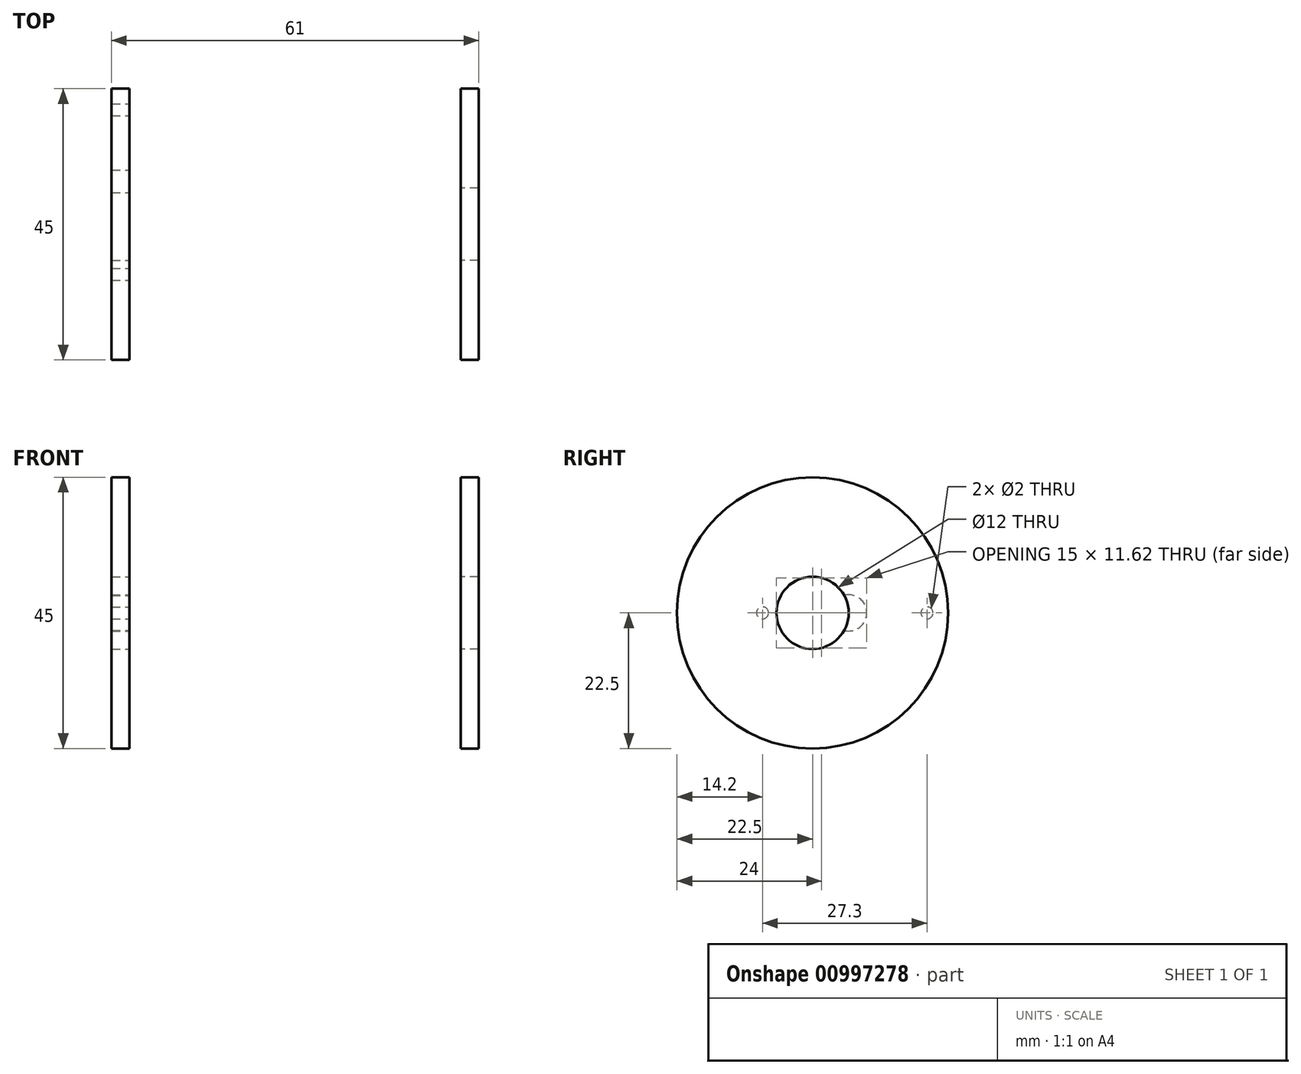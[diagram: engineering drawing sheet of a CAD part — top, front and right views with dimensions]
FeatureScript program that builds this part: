
annotation { "Feature Type Name" : "Feature", "Feature Type Description" : "" }
export const myFeature = defineFeature(function(context is Context, id is Id, definition is map)
    precondition{}
    {
        {
            var Q0;
            Q0=qCreatedBy(makeId("Front.planeOp"),FACE);
            var sketch = newSketch(context, id + "F0", { "sketchPlane" : qUnion([Q0])});
            skLineSegment(sketch, "E0.bottom", {"start": v(-27.5, 22.5) * mm, "end": v(27.5, 22.5) * mm});
            skLineSegment(sketch, "E0.top", {"start": v(-27.5, -22.5) * mm, "end": v(27.5, -22.5) * mm});
            skLineSegment(sketch, "E0.left", {"start": v(-27.5, 22.5) * mm, "end": v(-27.5, -22.5) * mm});
            skLineSegment(sketch, "E0.right", {"start": v(27.5, 22.5) * mm, "end": v(27.5, -22.5) * mm});
            skSolve(sketch);
        }
        {
            var Q0;
            Q0=qCreatedBy(makeId("Front.planeOp"),FACE);
            var sketch = newSketch(context, id + "F1", { "sketchPlane" : qUnion([Q0])});
            skLineSegment(sketch, "E1.bottom", {"start": v(-30.5, 22.5) * mm, "end": v(-27.5, 22.5) * mm});
            skLineSegment(sketch, "E1.top", {"start": v(-30.5, -22.5) * mm, "end": v(-27.5, -22.5) * mm});
            skLineSegment(sketch, "E1.left", {"start": v(-30.5, 22.5) * mm, "end": v(-30.5, -22.5) * mm});
            skLineSegment(sketch, "E1.right", {"start": v(-27.5, 22.5) * mm, "end": v(-27.5, -22.5) * mm});
            skLineSegment(sketch, "E2.bottom", {"start": v(27.5, 22.5) * mm, "end": v(30.5, 22.5) * mm});
            skLineSegment(sketch, "E2.top", {"start": v(27.5, -22.5) * mm, "end": v(30.5, -22.5) * mm});
            skLineSegment(sketch, "E2.left", {"start": v(27.5, 22.5) * mm, "end": v(27.5, -22.5) * mm});
            skLineSegment(sketch, "E2.right", {"start": v(30.5, 22.5) * mm, "end": v(30.5, -22.5) * mm});
            skSolve(sketch);
        }
        {
            var Q0;
            Q0 = qSketchRegion(id + "F1", true);
            extrude(context, id + "F2", {"entities" : qUnion([Q0]), "depth" : 45 * mm, "offsetDistance" : 25 * mm});
        }
        {
            var Q0;
            Q0=makeQuery(id+"F2.opExtrude","CAP_EDGE",EDGE,{"disambiguationData":[OSD([sQuery(id+"F1.wireOp",EDGE,"E1.bottom")])],"isStart":false});
            var Q1;
            Q1=makeQuery(id+"F2.opExtrude","CAP_EDGE",EDGE,{"disambiguationData":[OSD([sQuery(id+"F1.wireOp",EDGE,"E1.top")])],"isStart":false});
            var Q2;
            Q2=makeQuery(id+"F2.opExtrude","CAP_EDGE",EDGE,{"disambiguationData":[OSD([sQuery(id+"F1.wireOp",EDGE,"E1.top")])],"isStart":true});
            var Q3;
            Q3=makeQuery(id+"F2.opExtrude","CAP_EDGE",EDGE,{"disambiguationData":[OSD([sQuery(id+"F1.wireOp",EDGE,"E1.bottom")])],"isStart":true});
            fillet(context, id + "F3", {"entities" : qUnion([Q0, Q1, Q2, Q3]), "tangentPropagation" : true, "radius" : 22.5 * mm, "defaultsChanged" : false, "vertexSettings" : [], "allowEdgeOverflow" : false});
        }
        {
            var Q0;
            Q0=makeQuery(id+"F2.opExtrude","CAP_EDGE",EDGE,{"disambiguationData":[OSD([sQuery(id+"F1.wireOp",EDGE,"E2.top")])],"isStart":false});
            var Q1;
            Q1=makeQuery(id+"F2.opExtrude","CAP_EDGE",EDGE,{"disambiguationData":[OSD([sQuery(id+"F1.wireOp",EDGE,"E2.top")])],"isStart":true});
            var Q2;
            Q2=makeQuery(id+"F2.opExtrude","CAP_EDGE",EDGE,{"disambiguationData":[OSD([sQuery(id+"F1.wireOp",EDGE,"E2.bottom")])],"isStart":true});
            var Q3;
            Q3=makeQuery(id+"F2.opExtrude","CAP_EDGE",EDGE,{"disambiguationData":[OSD([sQuery(id+"F1.wireOp",EDGE,"E2.bottom")])],"isStart":false});
            fillet(context, id + "F4", {"entities" : qUnion([Q0, Q1, Q2, Q3]), "tangentPropagation" : true, "radius" : 22.5 * mm, "defaultsChanged" : false, "vertexSettings" : [], "allowEdgeOverflow" : false});
        }
        {
            var Q0;
            Q0=qCreatedBy(makeId("Right.planeOp"),FACE);
            var sketch = newSketch(context, id + "F5", { "sketchPlane" : qUnion([Q0])});
            skCircle(sketch, "E3", {"center": v(-22.5, 0) * mm, "radius": 6 * mm});
            skCircle(sketch, "E4", {"center": v(-22.5, 0) * mm, "radius": 3 * mm});
            skCircle(sketch, "E5", {"center": v(-16.5, 0) * mm, "radius": 3 * mm});
            skPoint(sketch, "E6", {"position": v(-3.5, 0) * mm});
            skPoint(sketch, "E7", {"position": v(-30.8, 0) * mm});
            skSolve(sketch);
        }
        {
            var Q0;
            Q0=sQuery(id+"F5.wireOp",VERTEX,"E3.center");
            var Q1;
            Q1=makeQuery(id+"F2.opExtrude","SWEPT_BODY",BODY,{"disambiguationData":[OSD([sQuery(id+"F1.wireOp",EDGE,"E2.bottom"),sQuery(id+"F1.wireOp",EDGE,"E2.top"),sQuery(id+"F1.wireOp",EDGE,"E2.left"),sQuery(id+"F1.wireOp",EDGE,"E2.right")])]});
            hole(context, id + "F6", {"style" : HoleStyle.SIMPLE, "endStyle" : HoleEndStyle.THROUGH, "oppositeDirection" : true, "holeDiameter" : 12 * mm, "majorDiameter" : 5 * mm, "isTappedThrough" : true, "tappedDepth" : 12 * mm, "tapClearance" : 3, "startFromSketch" : true, "locations" : qUnion([Q0]), "scope" : qUnion([Q1])});
        }
        {
            var Q0;
            Q0=sQuery(id+"F5.wireOp",VERTEX,"E3.center");
            var Q1;
            Q1=makeQuery(id+"F2.opExtrude","SWEPT_BODY",BODY,{"disambiguationData":[OSD([sQuery(id+"F1.wireOp",EDGE,"E1.bottom"),sQuery(id+"F1.wireOp",EDGE,"E1.top"),sQuery(id+"F1.wireOp",EDGE,"E1.left"),sQuery(id+"F1.wireOp",EDGE,"E1.right")])]});
            hole(context, id + "F7", {"style" : HoleStyle.SIMPLE, "endStyle" : HoleEndStyle.THROUGH, "holeDiameter" : 12 * mm, "majorDiameter" : 5 * mm, "isTappedThrough" : true, "tappedDepth" : 12 * mm, "tapClearance" : 3, "startFromSketch" : true, "locations" : qUnion([Q0]), "scope" : qUnion([Q1])});
        }
        {
            var Q0;
            Q0=sQuery(id+"F5.wireOp",VERTEX,"E5.center");
            var Q1;
            Q1=makeQuery(id+"F2.opExtrude","SWEPT_BODY",BODY,{"disambiguationData":[OSD([sQuery(id+"F1.wireOp",EDGE,"E1.bottom"),sQuery(id+"F1.wireOp",EDGE,"E1.top"),sQuery(id+"F1.wireOp",EDGE,"E1.left"),sQuery(id+"F1.wireOp",EDGE,"E1.right")])]});
            hole(context, id + "F8", {"style" : HoleStyle.SIMPLE, "endStyle" : HoleEndStyle.THROUGH, "holeDiameter" : 6 * mm, "majorDiameter" : 5 * mm, "isTappedThrough" : true, "tappedDepth" : 12 * mm, "tapClearance" : 3, "startFromSketch" : true, "locations" : qUnion([Q0]), "scope" : qUnion([Q1])});
        }
        {
            var Q0;
            Q0=sQuery(id+"F5.wireOp",VERTEX,"E6");
            var Q1;
            Q1=sQuery(id+"F5.wireOp",VERTEX,"E7");
            var Q2;
            Q2=makeQuery(id+"F2.opExtrude","SWEPT_BODY",BODY,{"disambiguationData":[OSD([sQuery(id+"F1.wireOp",EDGE,"E1.bottom"),sQuery(id+"F1.wireOp",EDGE,"E1.top"),sQuery(id+"F1.wireOp",EDGE,"E1.left"),sQuery(id+"F1.wireOp",EDGE,"E1.right")])]});
            hole(context, id + "F9", {"style" : HoleStyle.SIMPLE, "endStyle" : HoleEndStyle.THROUGH, "holeDiameter" : 2 * mm, "majorDiameter" : 5 * mm, "isTappedThrough" : true, "tappedDepth" : 12 * mm, "tapClearance" : 3, "startFromSketch" : true, "locations" : qUnion([Q0, Q1]), "scope" : qUnion([Q2])});
        }
    });
